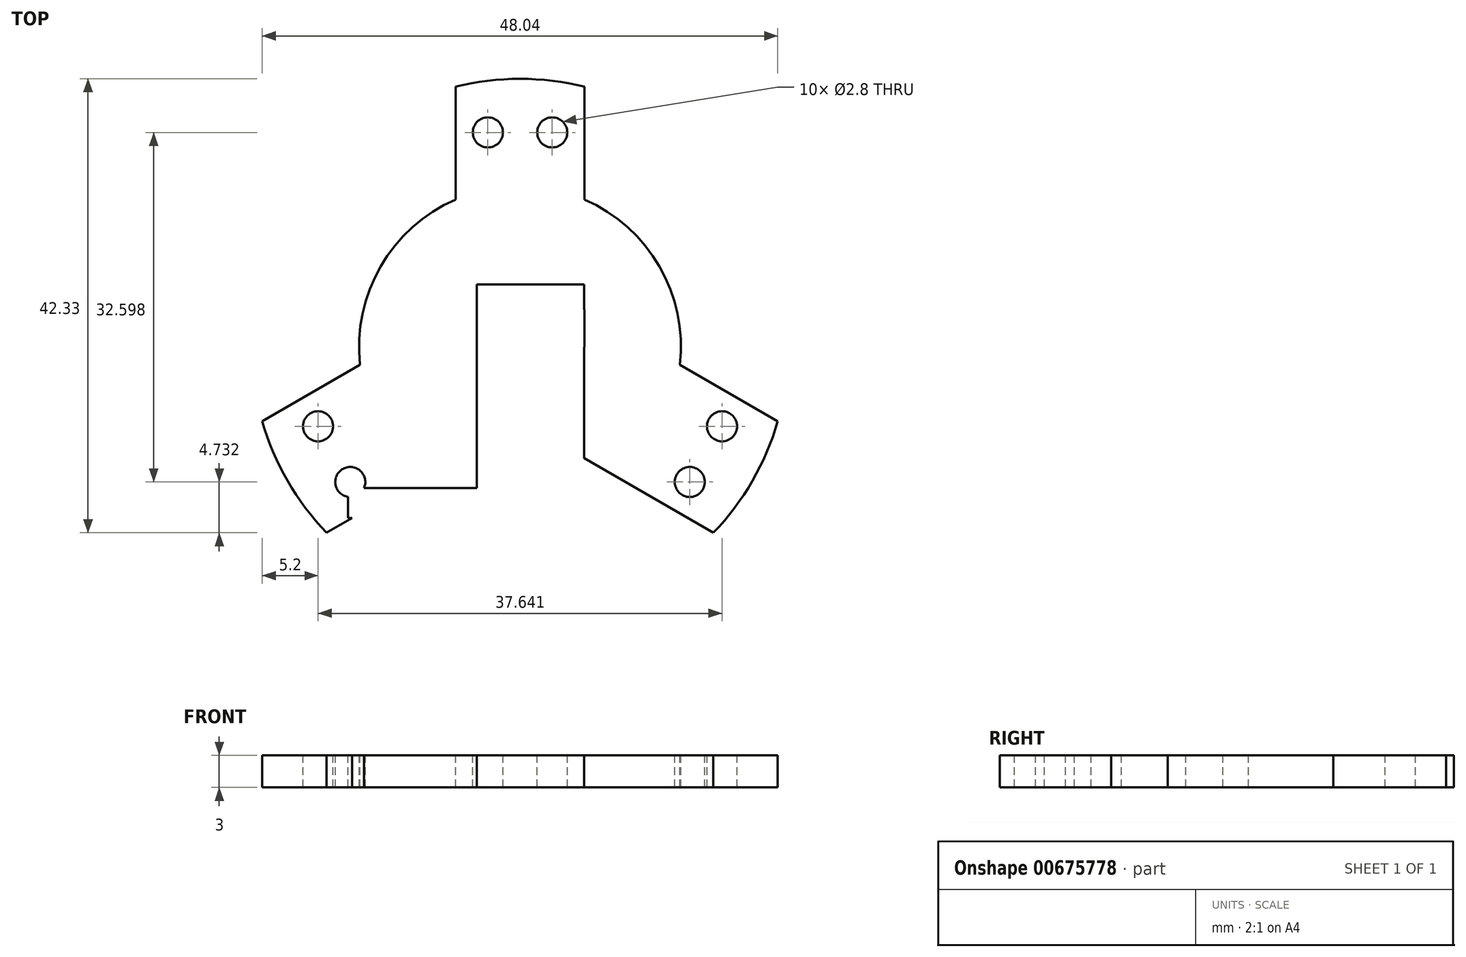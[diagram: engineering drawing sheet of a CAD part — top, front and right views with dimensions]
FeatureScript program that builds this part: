
annotation { "Feature Type Name" : "Feature", "Feature Type Description" : "" }
export const myFeature = defineFeature(function(context is Context, id is Id, definition is map)
    precondition{}
    {
        {
            var Q0;
            Q0=qCreatedBy(makeId("Top.planeOp"),FACE);
            var sketch = newSketch(context, id + "F0", { "sketchPlane" : qUnion([Q0])});
            skLineSegment(sketch, "E0.bottom", {"start": v(0, 0) * mm, "end": v(3.16, 0) * mm});
            skLineSegment(sketch, "E0.top", {"start": v(0, 3.16) * mm, "end": v(3.16, 3.16) * mm});
            skLineSegment(sketch, "E0.left", {"start": v(0, 0) * mm, "end": v(0, 3.16) * mm});
            skLineSegment(sketch, "E0.right", {"start": v(3.16, 0) * mm, "end": v(3.16, 3.16) * mm});
            skLineSegment(sketch, "E1.MirrorCS", {"start": v(-3.16, 0) * mm, "end": v(-3.16, 3.16) * mm});
            skLineSegment(sketch, "E2.MirrorCS", {"start": v(0, 3.16) * mm, "end": v(-3.16, 3.16) * mm});
            skLineSegment(sketch, "E3.MirrorCS", {"start": v(-3.16, 0) * mm, "end": v(-3.16, -3.16) * mm});
            skLineSegment(sketch, "E4.MirrorCS", {"start": v(0, -3.16) * mm, "end": v(-3.16, -3.16) * mm});
            skLineSegment(sketch, "E5.MirrorCS", {"start": v(0, -3.16) * mm, "end": v(3.16, -3.16) * mm});
            skLineSegment(sketch, "E6.MirrorCS", {"start": v(3.16, 0) * mm, "end": v(3.16, -3.16) * mm});
            skLineSegment(sketch, "E7.bottom", {"start": v(-4.04, 5.84) * mm, "end": v(5.96, 5.84) * mm});
            skLineSegment(sketch, "E7.top", {"start": v(-4.04, -11.16) * mm, "end": v(5.96, -11.16) * mm});
            skLineSegment(sketch, "E7.left", {"start": v(-4.04, 5.84) * mm, "end": v(-4.04, -11.16) * mm});
            skLineSegment(sketch, "E7.right", {"start": v(5.96, 5.84) * mm, "end": v(5.96, 3.49) * mm});
            skCircle(sketch, "E8", {"center": v(0, 0) * mm, "radius": 25 * mm});
            skLineSegment(sketch, "E9", {"start": v(0, 0) * mm, "end": v(0, 25) * mm});
            skLineSegment(sketch, "E10.bottom", {"start": v(-6, 0) * mm, "end": v(6, 0) * mm});
            skLineSegment(sketch, "E10.top", {"start": v(-6, 24.27) * mm, "end": v(6, 24.27) * mm});
            skLineSegment(sketch, "E10.left", {"start": v(-6, 3.46) * mm, "end": v(-6, 24.27) * mm});
            skLineSegment(sketch, "E10.right", {"start": v(6, 0) * mm, "end": v(6, 24.27) * mm});
            skArc(sketch, "E11.MirrorC", {"start": v(25, 0) * mm, "mid": v(-19.69, -15.41) * mm, "end": v(6, 24.27) * mm});
            skLineSegment(sketch, "E12", {"start": v(0, 0) * mm, "end": v(21.65, -12.5) * mm, "construction": true});
            skLineSegment(sketch, "E13", {"start": v(0, 0) * mm, "end": v(-21.65, -12.5) * mm, "construction": true});
            skLineSegment(sketch, "E14.top", {"start": v(24.02, -6.94) * mm, "end": v(18.02, -17.33) * mm});
            skLineSegment(sketch, "E14.left", {"start": v(5.96, 3.49) * mm, "end": v(24.02, -6.94) * mm});
            skLineSegment(sketch, "E14.right", {"start": v(0, -6.93) * mm, "end": v(18.02, -17.33) * mm});
            skLineSegment(sketch, "E15.top", {"start": v(-18.02, -17.33) * mm, "end": v(-24.02, -6.94) * mm});
            skLineSegment(sketch, "E15.left", {"start": v(0, -6.93) * mm, "end": v(-18.02, -17.33) * mm});
            skLineSegment(sketch, "E15.right", {"start": v(-2.95, 5.22) * mm, "end": v(-4.04, 4.6) * mm});
            skLineSegment(sketch, "E16.trimOffspring", {"start": v(-6, 3.46) * mm, "end": v(-24.02, -6.94) * mm});
            skPoint(sketch, "E17.orphan", {"position": v(3.16, 5.1) * mm});
            skLineSegment(sketch, "E18.trimOffspring", {"start": v(5.96, 0) * mm, "end": v(5.96, -11.16) * mm});
            skCircle(sketch, "E19", {"center": v(0, 0) * mm, "radius": 15 * mm});
            skArc(sketch, "E20", {"start": v(18.02, -17.33) * mm, "mid": v(21.65, -12.5) * mm, "end": v(24.02, -6.94) * mm});
            skLineSegment(sketch, "E21", {"start": v(-4.04, -11.16) * mm, "end": v(-4.04, -14.45) * mm});
            skLineSegment(sketch, "E22", {"start": v(5.96, -11.16) * mm, "end": v(5.96, -13.77) * mm});
            skLineSegment(sketch, "E23", {"start": v(5.96, -13.16) * mm, "end": v(-16.04, -13.16) * mm});
            skLineSegment(sketch, "E24.bottom", {"start": v(-16.04, -13.16) * mm, "end": v(5.96, -13.16) * mm});
            skLineSegment(sketch, "E24.top", {"start": v(-16.04, -15.96) * mm, "end": v(5.96, -15.96) * mm});
            skLineSegment(sketch, "E24.left", {"start": v(-16.04, -13.16) * mm, "end": v(-16.04, -15.96) * mm});
            skLineSegment(sketch, "E24.right", {"start": v(5.96, -13.16) * mm, "end": v(5.96, -15.96) * mm});
            skCircle(sketch, "E25", {"center": v(-3, 20) * mm, "radius": 1.4 * mm});
            skCircle(sketch, "E26.MirrorC", {"center": v(3, 20) * mm, "radius": 1.4 * mm});
            skCircle(sketch, "E27.MirrorC", {"center": v(-15.82, -12.6) * mm, "radius": 1.4 * mm});
            skCircle(sketch, "E28.MirrorC", {"center": v(-18.82, -7.4) * mm, "radius": 1.4 * mm});
            skCircle(sketch, "E29.MirrorC", {"center": v(15.82, -12.6) * mm, "radius": 1.4 * mm});
            skCircle(sketch, "E30.MirrorC", {"center": v(18.82, -7.4) * mm, "radius": 1.4 * mm});
            skSolve(sketch);
        }
        {
            var Q0;
            {var subQ0=sQuery(id+"F0.wireOp",EDGE,"E15.top");Q0=makeQuery(id+"F0.imprint","IMPRINT",FACE,{"disambiguationData":[TD([[makeQuery(id+"F0.imprint","IMPRINT",EDGE,{"derivedFrom":subQ0}),1.0]])]});}
            var Q1;
            {var subQ0=sQuery(id+"F0.wireOp",EDGE,"E9");var subQ1=sQuery(id+"F0.wireOp",EDGE,"E8");var subQ2=makeQuery(id+"F0.imprint","INTERSECT",VERTEX,{"derivedFrom":[subQ1,subQ0]});Q1=makeQuery(id+"F0.imprint","IMPRINT",FACE,{"disambiguationData":[TD([[makeQuery(id+"F0.imprint","IMPRINT",EDGE,{"disambiguationData":[TD([[subQ2,1.0]])],"derivedFrom":subQ0}),-1.0]])]});}
            var Q2;
            {var subQ0=sQuery(id+"F0.wireOp",EDGE,"E9");var subQ1=sQuery(id+"F0.wireOp",EDGE,"E8");var subQ2=makeQuery(id+"F0.imprint","INTERSECT",VERTEX,{"derivedFrom":[subQ1,subQ0]});Q2=makeQuery(id+"F0.imprint","IMPRINT",FACE,{"disambiguationData":[TD([[makeQuery(id+"F0.imprint","IMPRINT",EDGE,{"disambiguationData":[TD([[subQ2,1.0]])],"derivedFrom":subQ0}),1.0]])]});}
            var Q3;
            {var subQ5=sQuery(id+"F0.wireOp",EDGE,"E7.right");Q3=makeQuery(id+"F0.imprint","IMPRINT",FACE,{"disambiguationData":[TD([[makeQuery(id+"F0.imprint","IMPRINT",EDGE,{"derivedFrom":subQ5}),1.0]])]});}
            var Q4;
            {var subQ11=sQuery(id+"F0.wireOp",EDGE,"E10.left");Q4=makeQuery(id+"F0.imprint","IMPRINT",FACE,{"disambiguationData":[TD([[makeQuery(id+"F0.imprint","IMPRINT",EDGE,{"derivedFrom":subQ11}),-1.0]])]});}
            var Q5;
            {var subQ1=sQuery(id+"F0.wireOp",EDGE,"E14.top");Q5=makeQuery(id+"F0.imprint","IMPRINT",FACE,{"disambiguationData":[TD([[makeQuery(id+"F0.imprint","IMPRINT",EDGE,{"derivedFrom":subQ1}),-1.0]])]});}
            var Q6;
            {var subQ0=sQuery(id+"F0.wireOp",EDGE,"E15.top");Q6=makeQuery(id+"F0.imprint","IMPRINT",FACE,{"disambiguationData":[TD([[makeQuery(id+"F0.imprint","IMPRINT",EDGE,{"derivedFrom":subQ0}),-1.0]])]});}
            var Q7;
            {var subQ0=sQuery(id+"F0.wireOp",EDGE,"E19");var subQ1=sQuery(id+"F0.wireOp",EDGE,"E9");var subQ2=makeQuery(id+"F0.imprint","INTERSECT",VERTEX,{"derivedFrom":[subQ1,subQ0]});Q7=makeQuery(id+"F0.imprint","IMPRINT",FACE,{"disambiguationData":[TD([[makeQuery(id+"F0.imprint","IMPRINT",EDGE,{"disambiguationData":[TD([[subQ2,-1.0]])],"derivedFrom":subQ1}),-1.0]])]});}
            var Q8;
            {var subQ6=sQuery(id+"F0.wireOp",EDGE,"E10.right");var subQ9=sQuery(id+"F0.wireOp",EDGE,"E10.bottom");var subQ11=makeQuery(id+"F0.imprint","INTERSECT",VERTEX,{"derivedFrom":[subQ9,subQ6]});Q8=makeQuery(id+"F0.imprint","IMPRINT",FACE,{"disambiguationData":[TD([[makeQuery(id+"F0.imprint","IMPRINT",EDGE,{"disambiguationData":[TD([[subQ11,1.0]])],"derivedFrom":subQ9}),-1.0]])]});}
            var Q9;
            {var subQ0=sQuery(id+"F0.wireOp",EDGE,"E7.left");var subQ1=makeQuery(id+"F0.imprint","IMPRINT",VERTEX,{"derivedFrom":subQ0});Q9=makeQuery(id+"F0.imprint","IMPRINT",FACE,{"disambiguationData":[TD([[makeQuery(id+"F0.imprint","IMPRINT",EDGE,{"disambiguationData":[TD([[subQ1,1.0]])],"derivedFrom":subQ0}),-1.0]])]});}
            var Q10;
            {var subQ0=sQuery(id+"F0.wireOp",EDGE,"E14.left");var subQ1=sQuery(id+"F0.wireOp",EDGE,"E10.right");var subQ2=makeQuery(id+"F0.imprint","INTERSECT",VERTEX,{"derivedFrom":[subQ1,subQ0]});Q10=makeQuery(id+"F0.imprint","IMPRINT",FACE,{"disambiguationData":[TD([[makeQuery(id+"F0.imprint","IMPRINT",EDGE,{"disambiguationData":[TD([[subQ2,-1.0]])],"derivedFrom":subQ1}),-1.0]])]});}
            var Q11;
            {var subQ0=sQuery(id+"F0.wireOp",EDGE,"E16.trimOffspring");var subQ1=sQuery(id+"F0.wireOp",EDGE,"E10.left");var subQ2=makeQuery(id+"F0.imprint","INTERSECT",VERTEX,{"derivedFrom":[subQ1,subQ0]});Q11=makeQuery(id+"F0.imprint","IMPRINT",FACE,{"disambiguationData":[TD([[makeQuery(id+"F0.imprint","IMPRINT",EDGE,{"disambiguationData":[TD([[subQ2,-1.0]])],"derivedFrom":subQ1}),1.0]])]});}
            var Q12;
            {var subQ0=sQuery(id+"F0.wireOp",EDGE,"E14.top");Q12=makeQuery(id+"F0.imprint","IMPRINT",FACE,{"disambiguationData":[TD([[makeQuery(id+"F0.imprint","IMPRINT",EDGE,{"derivedFrom":subQ0}),1.0]])]});}
            var Q13;
            {var subQ1=sQuery(id+"F0.wireOp",EDGE,"E15.left");var subQ6=sQuery(id+"F0.wireOp",EDGE,"E7.left");var subQ9=makeQuery(id+"F0.imprint","INTERSECT",VERTEX,{"derivedFrom":[subQ6,subQ1]});Q13=makeQuery(id+"F0.imprint","IMPRINT",FACE,{"disambiguationData":[TD([[makeQuery(id+"F0.imprint","IMPRINT",EDGE,{"disambiguationData":[TD([[subQ9,-1.0]])],"derivedFrom":subQ1}),1.0]])]});}
            var Q14;
            {var subQ0=sQuery(id+"F0.wireOp",EDGE,"E19");var subQ1=sQuery(id+"F0.wireOp",EDGE,"E15.left");var subQ2=makeQuery(id+"F0.imprint","INTERSECT",VERTEX,{"derivedFrom":[subQ1,subQ0]});Q14=makeQuery(id+"F0.imprint","IMPRINT",FACE,{"disambiguationData":[TD([[makeQuery(id+"F0.imprint","IMPRINT",EDGE,{"disambiguationData":[TD([[subQ2,-1.0]])],"derivedFrom":subQ1}),1.0]])]});}
            extrude(context, id + "F1", {"entities" : qUnion([Q0, Q1, Q2, Q3, Q4, Q5, Q6, Q7, Q8, Q9, Q10, Q11, Q12, Q13, Q14]), "oppositeDirection" : true, "depth" : 3 * mm, "offsetDistance" : 25 * mm});
        }
    });
